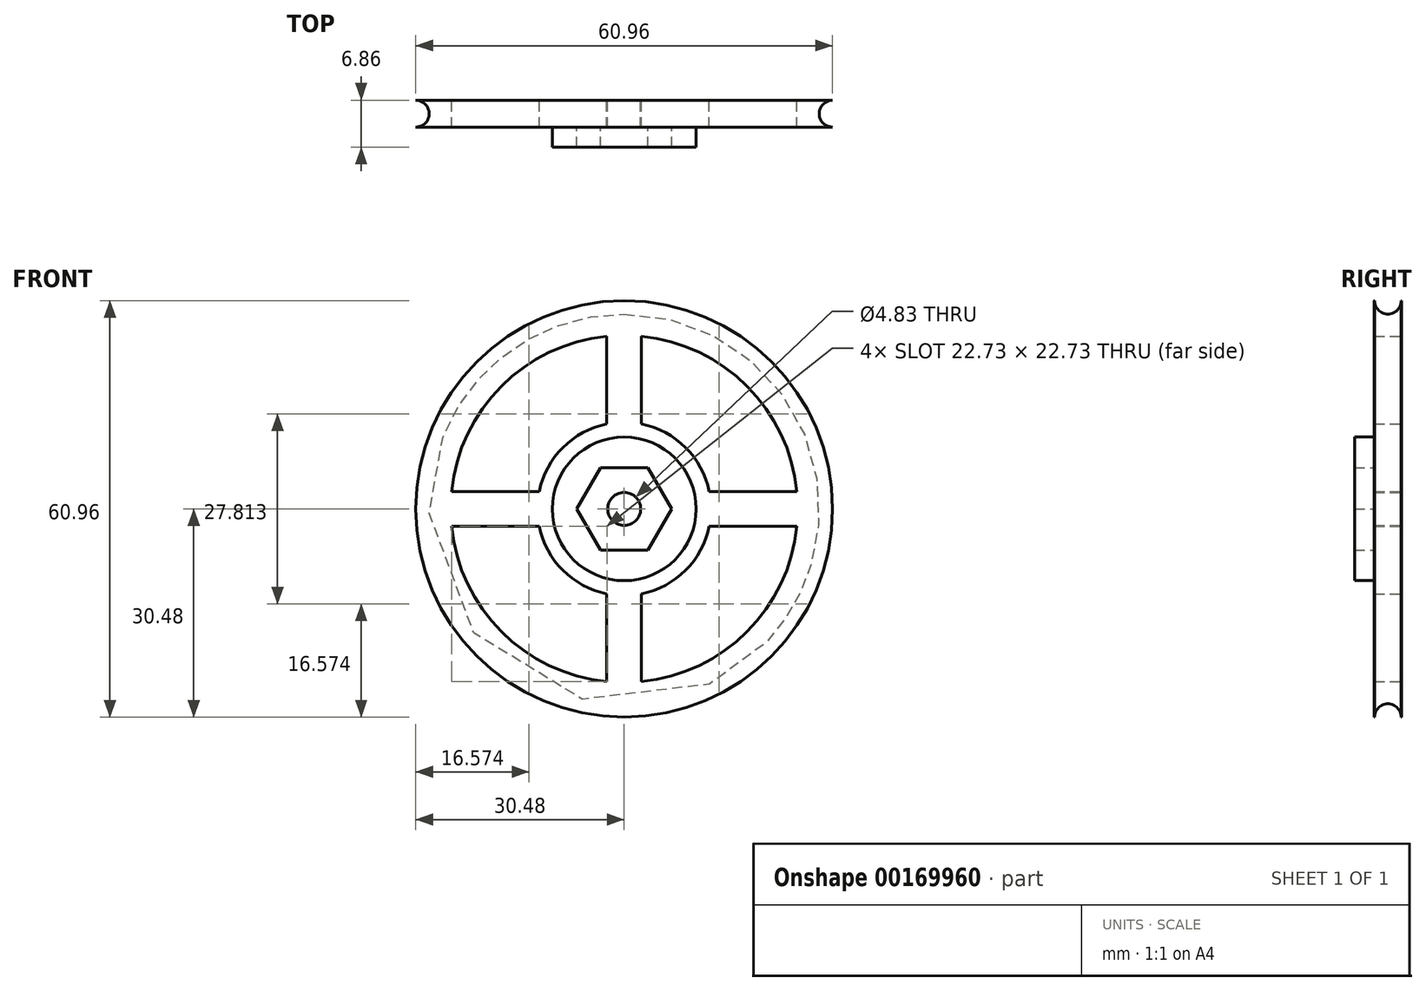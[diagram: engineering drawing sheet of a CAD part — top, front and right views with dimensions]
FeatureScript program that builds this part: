
annotation { "Feature Type Name" : "Feature", "Feature Type Description" : "" }
export const myFeature = defineFeature(function(context is Context, id is Id, definition is map)
    precondition{}
    {
        {
            var Q0;
            Q0=qCreatedBy(makeId("Front.planeOp"),FACE);
            var sketch = newSketch(context, id + "F0", { "sketchPlane" : qUnion([Q0])});
            skCircle(sketch, "E0", {"center": v(0, 0) * mm, "radius": 30.48 * mm});
            skCircle(sketch, "E1.cCircle", {"center": v(0, 0) * mm, "radius": 6.97 * mm, "construction": true});
            skLineSegment(sketch, "E1.0", {"start": v(3.48, 6.03) * mm, "end": v(6.97, 0) * mm});
            skLineSegment(sketch, "E1.1", {"start": v(6.97, 0) * mm, "end": v(3.48, -6.03) * mm});
            skLineSegment(sketch, "E1.2", {"start": v(3.48, -6.03) * mm, "end": v(-3.48, -6.03) * mm});
            skLineSegment(sketch, "E1.3", {"start": v(-3.48, -6.03) * mm, "end": v(-6.97, 0) * mm});
            skLineSegment(sketch, "E1.4", {"start": v(-6.97, 0) * mm, "end": v(-3.48, 6.03) * mm});
            skLineSegment(sketch, "E1.5", {"start": v(-3.48, 6.03) * mm, "end": v(3.48, 6.03) * mm});
            skCircle(sketch, "E2", {"center": v(0, 0) * mm, "radius": 10.5 * mm});
            skCircle(sketch, "E3", {"center": v(0, 0) * mm, "radius": 2.41 * mm});
            skArc(sketch, "E4", {"start": v(12.44, 2.54) * mm, "mid": v(8.98, 8.98) * mm, "end": v(2.54, 12.44) * mm});
            skLineSegment(sketch, "E5", {"start": v(12.44, 2.54) * mm, "end": v(25.27, 2.54) * mm});
            skArc(sketch, "E6", {"start": v(25.27, 2.54) * mm, "mid": v(17.96, 17.96) * mm, "end": v(2.54, 25.27) * mm});
            skLineSegment(sketch, "E7", {"start": v(2.54, 25.27) * mm, "end": v(2.54, 12.44) * mm});
            skArc(sketch, "E8", {"start": v(-2.54, 12.44) * mm, "mid": v(-8.98, 8.98) * mm, "end": v(-12.44, 2.54) * mm});
            skArc(sketch, "E9", {"start": v(-2.54, 25.27) * mm, "mid": v(-17.96, 17.96) * mm, "end": v(-25.27, 2.54) * mm});
            skArc(sketch, "E10", {"start": v(-12.44, -2.54) * mm, "mid": v(-8.98, -8.98) * mm, "end": v(-2.54, -12.44) * mm});
            skArc(sketch, "E11", {"start": v(-25.27, -2.54) * mm, "mid": v(-17.96, -17.96) * mm, "end": v(-2.54, -25.27) * mm});
            skArc(sketch, "E12", {"start": v(2.54, -12.44) * mm, "mid": v(8.98, -8.98) * mm, "end": v(12.44, -2.54) * mm});
            skArc(sketch, "E13", {"start": v(2.54, -25.27) * mm, "mid": v(17.96, -17.96) * mm, "end": v(25.27, -2.54) * mm});
            skLineSegment(sketch, "E14", {"start": v(-2.54, 25.27) * mm, "end": v(-2.54, 12.44) * mm});
            skLineSegment(sketch, "E15", {"start": v(-12.44, 2.54) * mm, "end": v(-25.27, 2.54) * mm});
            skLineSegment(sketch, "E16", {"start": v(-12.44, -2.54) * mm, "end": v(-25.27, -2.54) * mm});
            skLineSegment(sketch, "E17", {"start": v(-2.54, -12.44) * mm, "end": v(-2.54, -25.27) * mm});
            skLineSegment(sketch, "E18", {"start": v(2.54, -12.44) * mm, "end": v(2.54, -25.27) * mm});
            skLineSegment(sketch, "E19", {"start": v(12.44, -2.54) * mm, "end": v(25.27, -2.54) * mm});
            skSolve(sketch);
        }
        {
            var Q0;
            Q0=qSketchRegion(id+"F0",true);
            extrude(context, id + "F1", {"entities" : qUnion([Q0]), "depth" : 4 * mm});
        }
        {
            var Q0;
            Q0=qCreatedBy(makeId("Top.planeOp"),FACE);
            var sketch = newSketch(context, id + "F2", { "sketchPlane" : qUnion([Q0])});
            skCircle(sketch, "E20", {"center": v(30.48, -1.98) * mm, "radius": 1.96 * mm});
            skLineSegment(sketch, "E21", {"start": v(0, 0) * mm, "end": v(0, 17.77) * mm, "construction": true});
            skSolve(sketch);
        }
        {
            var Q0;
            Q0=qSketchRegion(id+"F2",true);
            var Q1;
            Q1=sQuery(id+"F2.wireOp",EDGE,"E21");
            revolve(context, id + "F3", {"operationType" : NewBodyOperationType.REMOVE, "entities" : qUnion([Q0]), "axis" : qUnion([Q1]), "revolveType" : RevolveType.FULL, "oppositeDirection" : true});
        }
        {
            var Q0;
            Q0=makeQuery(id+"F0.imprint","IMPRINT",FACE,{"disambiguationData":[TD([[makeQuery(id+"F0.imprint","IMPRINT",EDGE,{"derivedFrom":sQuery(id+"F0.wireOp",EDGE,"E1.0")}),1.0]])]});
            var Q1;
            Q1=makeQuery(id+"F0.imprint","IMPRINT",FACE,{"disambiguationData":[TD([[makeQuery(id+"F0.imprint","IMPRINT",EDGE,{"derivedFrom":sQuery(id+"F0.wireOp",EDGE,"E1.0")}),-1.0]])]});
            extrude(context, id + "F4", {"entities" : qUnion([Q0, Q1]), "operationType" : NewBodyOperationType.ADD, "depth" : 4 * mm});
        }
        {
            var Q0;
            Q0=makeQuery(id+"F0.imprint","IMPRINT",FACE,{"disambiguationData":[TD([[makeQuery(id+"F0.imprint","IMPRINT",EDGE,{"derivedFrom":sQuery(id+"F0.wireOp",EDGE,"E1.0")}),1.0]])]});
            extrude(context, id + "F5", {"entities" : qUnion([Q0]), "operationType" : NewBodyOperationType.ADD, "depth" : 6.86 * mm});
        }
    });
